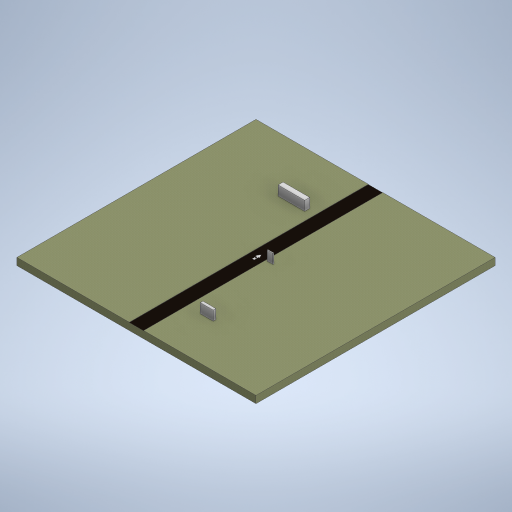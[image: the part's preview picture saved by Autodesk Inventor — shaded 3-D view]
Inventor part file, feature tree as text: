
AUTODESK INVENTOR PART (.ipt)
format: ipt  version: 2023 (Build 270158000, 158)  size: 309,760 bytes
history: native  units: in
note: dims shown in document units (in); Inventor stores cm internally (conversion verified against a paired STEP export)
features: extrude x5, sketch x5, pattern_linear x2, projected_geometry x1
ambient origin geometry x8: Origin, YZ Plane, XZ Plane, XY Plane, X Axis, Y Axis, Z Axis, Center Point
bodies: Solid1 (feature_tree)
feature tree (13):
  extrude  "Extrusion1"  Depth=3937.0079in
  extrude  "Extrusion2"  Depth=236.2205in
  extrude  "Extrusion3"  Depth=157.4803in
  pattern_linear  "Rectangular Pattern1"  Count1=50 Spacing1=0.0in
  pattern_linear  "Rectangular Pattern2"  Count1=2  [1 undecoded]
  extrude  "Extrusion4"  Depth=39.3701in
  extrude  "Extrusion5"  Depth=0.0394in TaperAngle=0.0deg
  sketch  "Sketch1"  dims[d0=3937.0079in d1=3937.0079in]
  sketch  "Sketch2"  dims[d2=118.1102in d3=0.0in d4=236.2205in]
  sketch  "Sketch3"  dims[d5=3.937in d6=0.0in d7=19.685in d8=19.685in d9=157.4803in d10=0.0in d11=0.7874in d13=472.4409in]
  projected_geometry  "Projected Loop1"
  sketch  "Sketch4"  dims[d14=0.7874in d16=472.4409in d17=39.3701in]
  sketch  "Sketch5"  dims[d18=157.4803in d19=0.0in d20=0.0394in d21=0.0in d23=19.685in]
note: 1 required parameter value undecoded (feature->parameter linkage not recoverable at this tier; creation-order binding heuristic only, values carry confidence <= 0.55)
